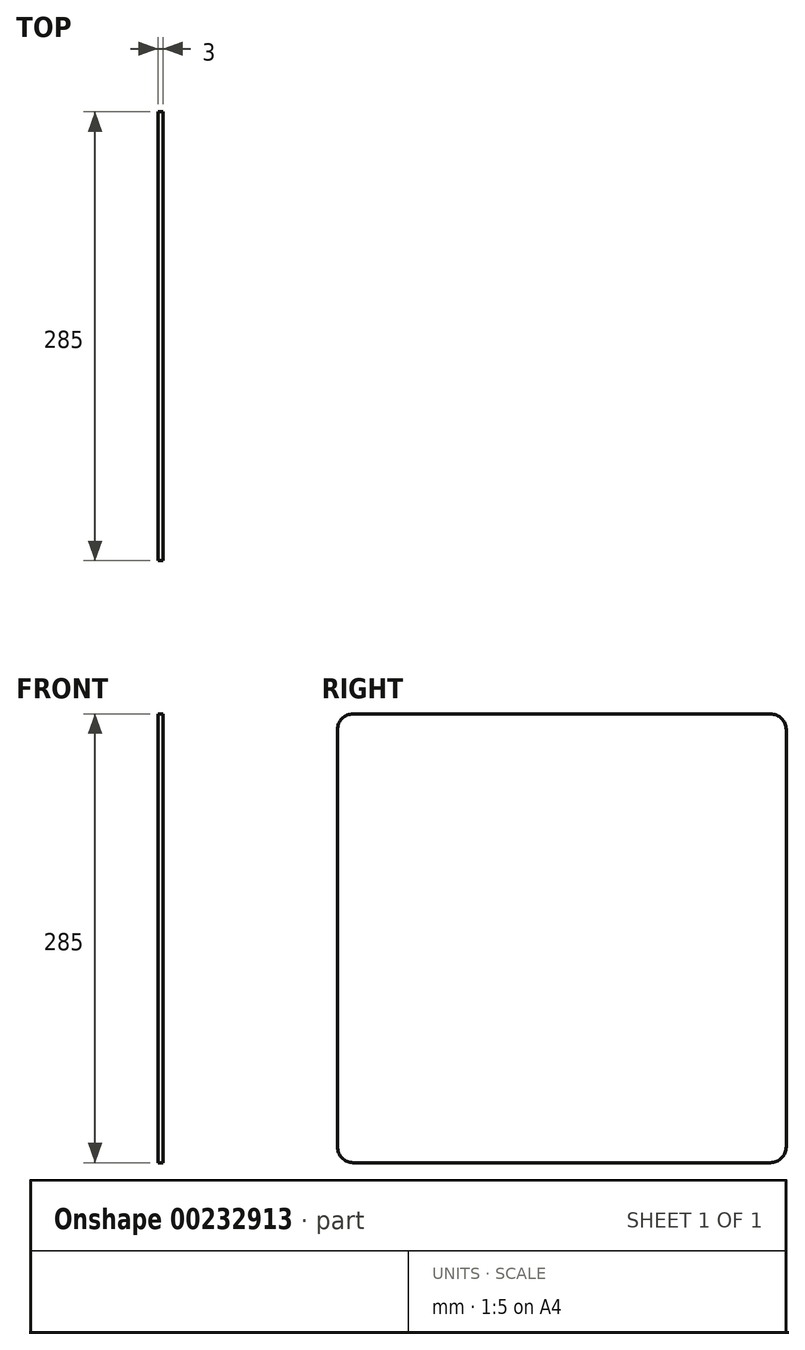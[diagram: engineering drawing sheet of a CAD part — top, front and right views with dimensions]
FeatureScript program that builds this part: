
annotation { "Feature Type Name" : "Feature", "Feature Type Description" : "" }
export const myFeature = defineFeature(function(context is Context, id is Id, definition is map)
    precondition{}
    {
        {
            var Q0;
            Q0=qCreatedBy(makeId("Right.planeOp"),FACE);
            var sketch = newSketch(context, id + "F0", { "sketchPlane" : qUnion([Q0])});
            skLineSegment(sketch, "E0.bottom", {"start": v(-132.5, 142.5) * mm, "end": v(132.5, 142.5) * mm});
            skLineSegment(sketch, "E0.top", {"start": v(-132.5, -142.5) * mm, "end": v(132.5, -142.5) * mm});
            skLineSegment(sketch, "E0.left", {"start": v(-142.5, 132.5) * mm, "end": v(-142.5, -132.5) * mm});
            skLineSegment(sketch, "E0.right", {"start": v(142.5, 132.5) * mm, "end": v(142.5, -132.5) * mm});
            skPoint(sketch, "E0.middle", {"position": v(0, 0) * mm});
            skPoint(sketch, "E1.visualSharp", {"position": v(-142.5, 142.5) * mm});
            skArc(sketch, "E1.filletArc", {"start": v(-132.5, 142.5) * mm, "mid": v(-139.57, 139.57) * mm, "end": v(-142.5, 132.5) * mm});
            skPoint(sketch, "E2.visualSharp", {"position": v(-142.5, -142.5) * mm});
            skArc(sketch, "E2.filletArc", {"start": v(-142.5, -132.5) * mm, "mid": v(-139.57, -139.57) * mm, "end": v(-132.5, -142.5) * mm});
            skPoint(sketch, "E3.visualSharp", {"position": v(142.5, -142.5) * mm});
            skArc(sketch, "E3.filletArc", {"start": v(132.5, -142.5) * mm, "mid": v(139.57, -139.57) * mm, "end": v(142.5, -132.5) * mm});
            skPoint(sketch, "E4.visualSharp", {"position": v(142.5, 142.5) * mm});
            skArc(sketch, "E4.filletArc", {"start": v(142.5, 132.5) * mm, "mid": v(139.57, 139.57) * mm, "end": v(132.5, 142.5) * mm});
            skSolve(sketch);
        }
        {
            var Q0;
            Q0 = qSketchRegion(id + "F0", true);
            extrude(context, id + "F1", {"entities" : qUnion([Q0]), "depth" : 3 * mm});
        }
    });
